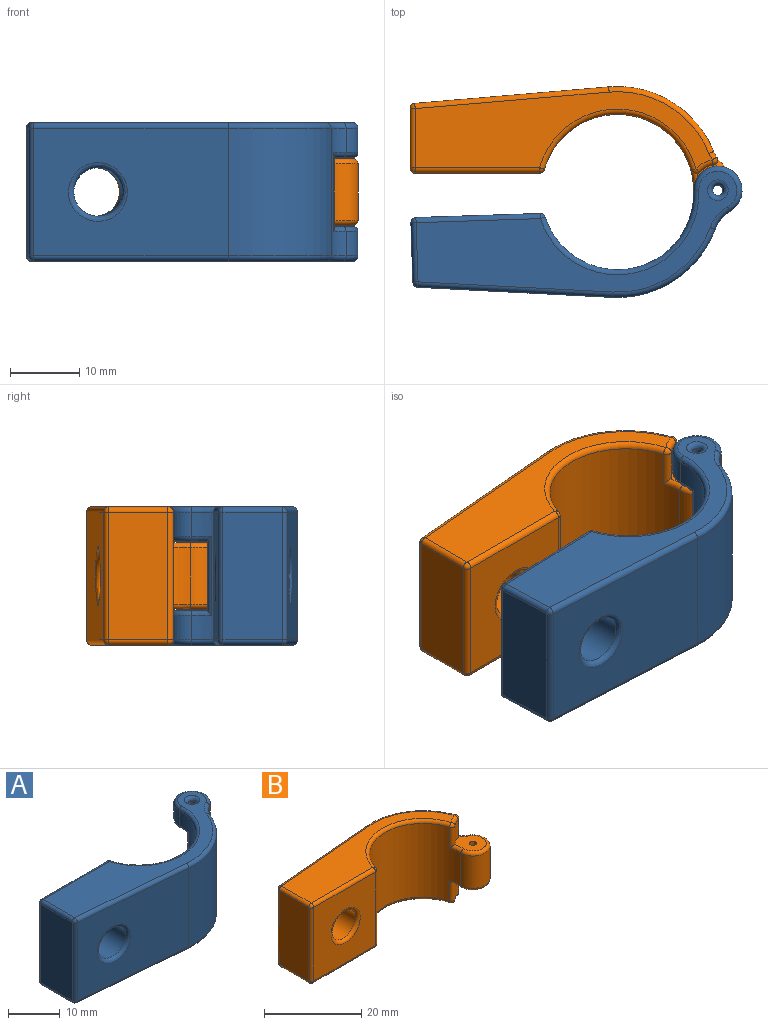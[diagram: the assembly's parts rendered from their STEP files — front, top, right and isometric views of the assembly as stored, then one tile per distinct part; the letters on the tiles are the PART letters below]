
ASSEMBLY  parts=2 mates=1
PART A: 51 faces, bbox 48.3x20x20 mm
  f0: plane 6.52x5.75mm, normal (0,0,1), area 25.6mm2, adj f7,f9,f18,f20,f21,f22,f23
  f1: plane 28.04x18.5mm, normal (-0.08,-1,0), area 463.7mm2, adj f2,f28,f36,f42,f47
  f2: cylinder r=15mm len=18.5mm, axis (0,0,1), area 353.2mm2, adj f1,f15,f25,f44
  f3: cylinder r=3.5mm len=7mm, axis (0,0,1), area 51.6mm2, adj f4,f15,f22,f27
  f4: cylinder r=11mm len=21.57mm, axis (0,0,1), area 548.3mm2, adj f3,f11,f16,f18,f20,f32,f39,f43
  f5: plane 18.5x17.96mm, normal (0,1,0), area 275.5mm2, adj f30,f31,f38,f39,f48
  f6: plane 18.5x8.56mm, normal (-1,0,0), area 158.4mm2, adj f29,f30,f36,f37
  f7: cylinder r=0.75mm len=4.25mm, axis (0,0,1), area 20mm2, adj f0,f49
  f8: plane 46.5x17mm, normal (0,0,-1), area 279.9mm2, adj f24,f25,f27,f28,f29,f31,f32,f49
  f9: cylinder r=3.7mm len=10mm, axis (0,0,-1), area 22.7mm2, adj f0,f10,f18,f21
  f10: plane 6.52x5.75mm, normal (0,0,-1), area 25.6mm2, adj f9,f12,f16,f17,f18,f19,f21
  f11: cylinder r=3.5mm len=7mm, axis (0,0,-1), area 51.6mm2, adj f4,f15,f17,f45
  f12: cylinder r=0.75mm len=4.25mm, axis (0,0,-1), area 20mm2, adj f10,f50
  f13: plane 46.5x17mm, normal (0,0,1), area 279.9mm2, adj f37,f38,f42,f43,f44,f45,f46,f50
  f14: cylinder r=3.5mm len=9.72mm, axis (0,1,0), area 205.6mm2, adj f47,f48
  f15: cylinder r=5mm len=18.5mm, axis (0,0,1), area 34.8mm2, adj f2,f3,f11,f19,f21,f23,f24,f46
  f16: torus R=11.75mm, axis (0,0,1), area 3mm2, adj f4,f10,f17,f18
  f17: torus R=2.75mm, axis (0,0,1), area 16mm2, adj f10,f11,f16,f19
  f18: cylinder r=0.75mm len=11.5mm, axis (0,0,-1), area 16.3mm2, adj f0,f4,f9,f10,f16,f20
  f19: torus R=5.75mm, axis (0,0,1), area 2.6mm2, adj f10,f15,f17,f21
  f20: torus R=11.75mm, axis (0,0,-1), area 3mm2, adj f0,f4,f18,f22
  f21: cylinder r=0.75mm len=11.5mm, axis (0,0,-1), area 15.3mm2, adj f0,f9,f10,f15,f19,f23
  f22: torus R=2.75mm, axis (0,0,-1), area 16mm2, adj f0,f3,f20,f23
  f23: torus R=5.75mm, axis (0,0,-1), area 2.6mm2, adj f0,f15,f21,f22
  f24: torus R=5.75mm, axis (0,0,-1), area 4.3mm2, adj f8,f15,f25,f27
  f25: torus R=14.25mm, axis (0,0,-1), area 22.1mm2, adj f2,f8,f24,f28
  f26: sphere r=0.75mm, area 0.9mm2, adj f29,f30,f31
  f27: torus R=2.75mm, axis (0,0,-1), area 16mm2, adj f3,f8,f24,f32
  f28: cylinder r=0.75mm len=28.1mm, axis (-1,0.08,0), area 33.2mm2, adj f1,f8,f25,f33
  f29: cylinder r=0.75mm len=8.56mm, axis (0,1,0), area 10.1mm2, adj f6,f8,f26,f33
  f30: cylinder r=0.75mm len=18.5mm, axis (0,0,1), area 21.8mm2, adj f5,f6,f26,f34
  f31: cylinder r=0.75mm len=17.96mm, axis (1,0,0), area 21.2mm2, adj f5,f8,f26,f35
  f32: torus R=11.75mm, axis (0,0,-1), area 38mm2, adj f4,f8,f27,f35
  f33: sphere r=0.75mm, area 0.8mm2, adj f28,f29,f36
  f34: sphere r=0.75mm, area 0.9mm2, adj f30,f37,f38
  f35: sphere r=0.75mm, area 0.7mm2, adj f31,f32,f39
  f36: cylinder r=0.75mm len=18.5mm, axis (0,0,1), area 20.6mm2, adj f1,f6,f33,f40
  f37: cylinder r=0.75mm len=8.56mm, axis (0,1,0), area 10.1mm2, adj f6,f13,f34,f40
  f38: cylinder r=0.75mm len=17.96mm, axis (1,0,0), area 21.2mm2, adj f5,f13,f34,f41
  f39: cylinder r=0.75mm len=18.5mm, axis (0,0,1), area 17.9mm2, adj f4,f5,f35,f41
  f40: sphere r=0.75mm, area 0.8mm2, adj f36,f37,f42
  f41: sphere r=0.75mm, area 0.7mm2, adj f38,f39,f43
  f42: cylinder r=0.75mm len=28.1mm, axis (-1,0.08,0), area 33.2mm2, adj f1,f13,f40,f44
  f43: torus R=11.75mm, axis (0,0,1), area 38mm2, adj f4,f13,f41,f45
  f44: torus R=14.25mm, axis (0,0,1), area 22.1mm2, adj f2,f13,f42,f46
  f45: torus R=2.75mm, axis (0,0,1), area 16mm2, adj f11,f13,f43,f46
  f46: torus R=5.75mm, axis (0,0,1), area 4.3mm2, adj f13,f15,f44,f45
  f47: bspline ~8.5x8.49mm, area 28mm2, adj f1,f14
  f48: torus R=4.25mm, axis (0,1,0), area 27.9mm2, adj f5,f14
  f49: torus R=1.5mm, axis (0,0,-1), area 7.6mm2, adj f7,f8
  f50: torus R=1.5mm, axis (0,0,1), area 7.6mm2, adj f12,f13
PART B: 54 faces, bbox 48.3x20x20 mm
  f0: plane 6.52x5.75mm, normal (0,0,-1), area 25.6mm2, adj f7,f9,f46,f48,f49,f50,f51
  f1: cylinder r=11mm len=21.57mm, axis (0,0,-1), area 551.5mm2, adj f2,f22,f26,f34,f40,f45,f49,f51
  f2: cylinder r=3.5mm len=8.1mm, axis (0,0,-1), area 119.5mm2, adj f1,f14,f19,f50
  f3: cylinder r=15mm len=18.5mm, axis (0,0,-1), area 353.2mm2, adj f4,f14,f16,f38
  f4: plane 28.04x18.5mm, normal (-0.08,1,0), area 463.7mm2, adj f3,f20,f27,f35,f52
  f5: plane 18.5x8.56mm, normal (-1,0,0), area 158.4mm2, adj f24,f27,f31,f32
  f6: plane 18.5x17.96mm, normal (0,-1,0), area 275.5mm2, adj f32,f33,f39,f40,f53
  f7: cylinder r=0.75mm len=9.6mm, axis (0,0,-1), area 45.2mm2, adj f0,f10
  f8: plane 42.96x11.13mm, normal (0,0,-1), area 257.4mm2, adj f31,f35,f38,f39,f41,f44,f45
  f9: cylinder r=3.7mm len=4.45mm, axis (0,0,1), area 10.1mm2, adj f0,f44,f46,f49
  f10: plane 6.52x5.75mm, normal (0,0,1), area 25.6mm2, adj f7,f12,f15,f18,f19,f22,f26
  f11: plane 42.96x11.13mm, normal (0,0,1), area 257.4mm2, adj f16,f17,f20,f24,f25,f33,f34
  f12: cylinder r=3.7mm len=4.45mm, axis (0,0,-1), area 10.1mm2, adj f10,f18,f25,f26
  f13: cylinder r=3.5mm len=9.71mm, axis (0,1,0), area 205.6mm2, adj f52,f53
  f14: cylinder r=5mm len=18.5mm, axis (0,0,1), area 37.6mm2, adj f2,f3,f15,f17,f18,f41,f46,f48
  f15: torus R=5.75mm, axis (0,0,1), area 2.6mm2, adj f10,f14,f18,f19
  f16: torus R=14.25mm, axis (0,0,1), area 22.1mm2, adj f3,f11,f17,f20
  f17: torus R=5.75mm, axis (0,0,1), area 1.2mm2, adj f11,f14,f16,f21
  f18: cylinder r=0.75mm len=5.2mm, axis (0,0,1), area 6.8mm2, adj f10,f12,f14,f15,f21
  f19: torus R=2.75mm, axis (0,0,1), area 16mm2, adj f2,f10,f15,f22
  f20: cylinder r=0.75mm len=28.1mm, axis (-1,-0.08,0), area 33.2mm2, adj f4,f11,f16,f23
  f21: sphere r=0.75mm, area 1.1mm2, adj f17,f18,f25
  f22: torus R=11.75mm, axis (0,0,1), area 3mm2, adj f1,f10,f19,f26
  f23: sphere r=0.75mm, area 0.8mm2, adj f20,f24,f27
  f24: cylinder r=0.75mm len=8.56mm, axis (0,-1,0), area 10.1mm2, adj f5,f11,f23,f28
  f25: torus R=4.45mm, axis (0,0,1), area 2.9mm2, adj f11,f12,f21,f29
  f26: cylinder r=0.75mm len=5.2mm, axis (0,0,-1), area 7.3mm2, adj f1,f10,f12,f22,f29
  f27: cylinder r=0.75mm len=18.5mm, axis (0,0,-1), area 20.6mm2, adj f4,f5,f23,f30
  f28: sphere r=0.75mm, area 0.9mm2, adj f24,f32,f33
  f29: sphere r=0.75mm, area 1.2mm2, adj f25,f26,f34
  f30: sphere r=0.75mm, area 0.8mm2, adj f27,f31,f35
  f31: cylinder r=0.75mm len=8.56mm, axis (0,-1,0), area 10.1mm2, adj f5,f8,f30,f36
  f32: cylinder r=0.75mm len=18.5mm, axis (0,0,-1), area 21.8mm2, adj f5,f6,f28,f36
  f33: cylinder r=0.75mm len=17.96mm, axis (1,0,0), area 21.2mm2, adj f6,f11,f28,f37
  f34: torus R=11.75mm, axis (0,0,1), area 34.4mm2, adj f1,f11,f29,f37
  f35: cylinder r=0.75mm len=28.1mm, axis (-1,-0.08,0), area 33.2mm2, adj f4,f8,f30,f38
  f36: sphere r=0.75mm, area 0.9mm2, adj f31,f32,f39
  f37: sphere r=0.75mm, area 0.7mm2, adj f33,f34,f40
  f38: torus R=14.25mm, axis (0,0,-1), area 22.1mm2, adj f3,f8,f35,f41
  f39: cylinder r=0.75mm len=17.96mm, axis (1,0,0), area 21.2mm2, adj f6,f8,f36,f42
  f40: cylinder r=0.75mm len=18.5mm, axis (0,0,-1), area 17.9mm2, adj f1,f6,f37,f42
  f41: torus R=5.75mm, axis (0,0,-1), area 1.2mm2, adj f8,f14,f38,f43
  f42: sphere r=0.75mm, area 0.7mm2, adj f39,f40,f45
  f43: sphere r=0.75mm, area 1.1mm2, adj f41,f44,f46
  f44: torus R=4.45mm, axis (0,0,-1), area 2.9mm2, adj f8,f9,f43,f47
  f45: torus R=11.75mm, axis (0,0,-1), area 34.4mm2, adj f1,f8,f42,f47
  f46: cylinder r=0.75mm len=5.2mm, axis (0,0,1), area 6.8mm2, adj f0,f9,f14,f43,f48
  f47: sphere r=0.75mm, area 1.2mm2, adj f44,f45,f49
  f48: torus R=5.75mm, axis (0,0,-1), area 2.6mm2, adj f0,f14,f46,f50
  f49: cylinder r=0.75mm len=5.2mm, axis (0,0,1), area 7.3mm2, adj f0,f1,f9,f47,f51
  f50: torus R=2.75mm, axis (0,0,-1), area 16mm2, adj f0,f2,f48,f51
  f51: torus R=11.75mm, axis (0,0,-1), area 3mm2, adj f0,f1,f49,f50
  f52: bspline ~8.5x8.49mm, area 28mm2, adj f4,f13
  f53: torus R=4.25mm, axis (0,-1,0), area 27.9mm2, adj f6,f13
PLACE A rot(axis=(0,0,1),1.9deg) t=(16.86,10.96,-2.99)mm
PLACE B t=(16.86,11.44,-2.99)mm fixed
MATE revolute B.f9 <-> A.f9  axis (0,0,-1) through (31.36,11.44,-12.79)mm
